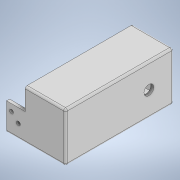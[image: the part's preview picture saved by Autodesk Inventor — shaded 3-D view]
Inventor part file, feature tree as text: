
AUTODESK INVENTOR PART (.ipt)
format: ipt  version: 2020 (Build 240168000, 168)  size: 273,920 bytes
history: native  units: in
note: dims shown in document units (in); Inventor stores cm internally (conversion verified against a paired STEP export)
features: extrude x13, sketch x13, fillet x1, mirror x1
ambient origin geometry x8: Origin, YZ Plane, XZ Plane, XY Plane, X Axis, Y Axis, Z Axis, Center Point
bodies: Solid1 (feature_tree)
feature tree (28):
  extrude  "Extrusion1"  Depth=4.3307in
  extrude  "Extrusion2"  Depth=1.6142in
  extrude  "Extrusion3"  Depth=1.6142in
  extrude  "Extrusion4"  Depth=0.1181in
  extrude  "Extrusion5"  Depth=0.1181in
  extrude  "Extrusion6"  Depth=0.9843in TaperAngle=0.0deg
  extrude  "Extrusion7"  Depth=1.8898in
  extrude  "Extrusion8"  Depth=0.1575in
  fillet  "Fillet1"  Radius=0.1181in
  extrude  "Extrusion9"  Depth=0.1575in
  extrude  "Extrusion10"  Depth=0.3937in
  mirror  "Mirror1"
  extrude  "Extrusion11"  Depth=0.1181in
  extrude  "Extrusion12"  Depth=0.1181in
  extrude  "Extrusion13"  Depth=0.7874in TaperAngle=0.0deg
  sketch  "Sketch1"  dims[d0=2.3622in d1=4.3307in]
  sketch  "Sketch2"  dims[d2=0.1181in d3=0.0in d4=1.6142in]
  sketch  "Sketch3"  dims[d5=0.1181in d6=1.6142in]
  sketch  "Sketch4"  dims[d7=0.1181in d8=0.1181in]
  sketch  "Sketch5"  dims[d9=1.8504in d10=0.0in d11=0.1181in]
  sketch  "Sketch6"  dims[d12=0.1181in d13=0.9843in d14=0.0in]
  sketch  "Sketch7"  dims[d15=1.1024in d16=1.8898in]
  sketch  "Sketch8"  dims[d17=0.1575in d18=0.1575in d19=0.1181in d20=0.0in]
  sketch  "Sketch9"  dims[d21=0.1575in d22=0.1575in]
  sketch  "Sketch10"  dims[d23=4.3307in d24=0.0in d25=0.3937in]
  sketch  "Sketch11"  dims[d26=0.1181in d27=0.0in d28=0.1181in]
  sketch  "Sketch12"  dims[d29=1.6142in d30=0.0in d31=0.1181in]
  sketch  "Sketch13"  dims[d32=4.0945in d33=0.7874in d34=0.0in d35=0.0787in d36=0.315in d37=0.315in d38=0.1181in d39=0.0in d40=0.2362in d41=0.2362in d42=0.1181in d43=0.0in d44=0.2362in d45=0.315in d46=0.2362in d47=0.315in d48=0.1181in d49=0.0in d50=0.3937in d51=0.1181in d52=0.1181in d53=0.0in d54=0.1181in d55=0.3937in d56=0.0in]
